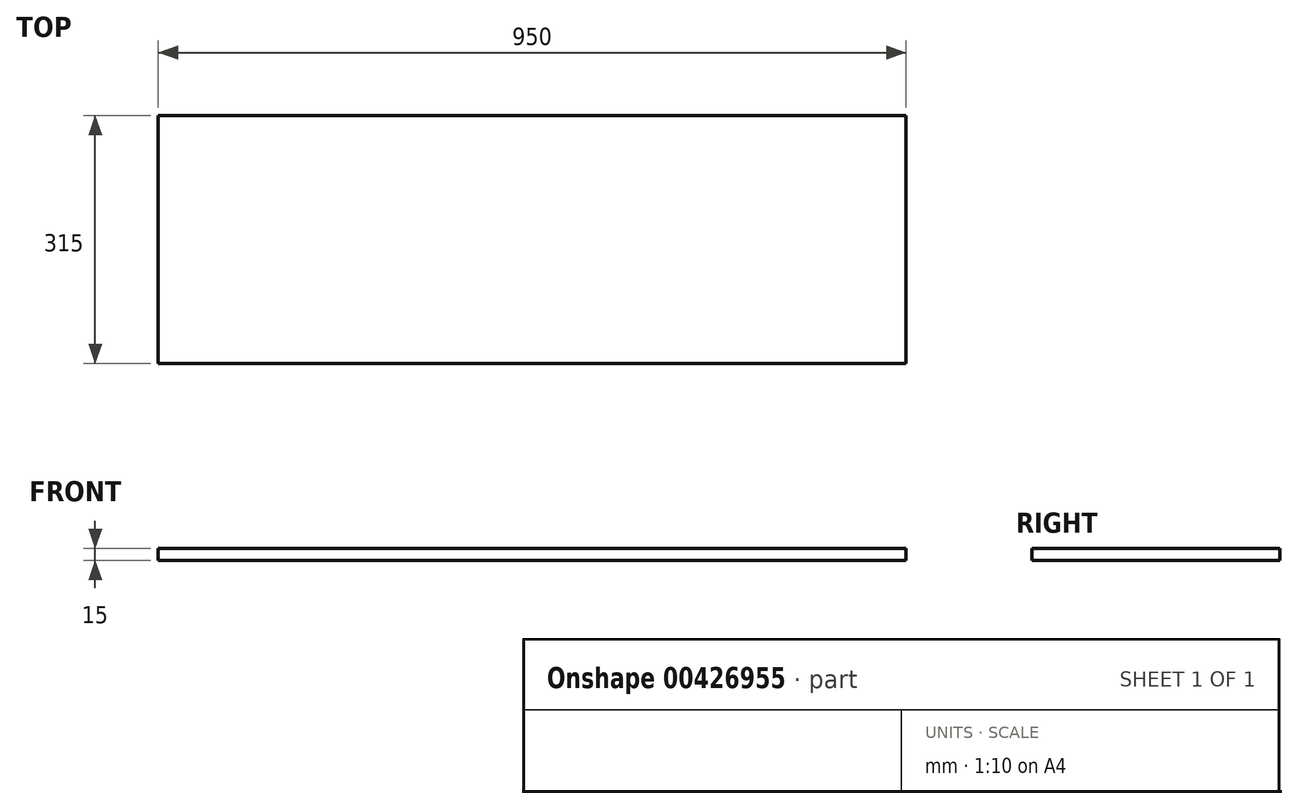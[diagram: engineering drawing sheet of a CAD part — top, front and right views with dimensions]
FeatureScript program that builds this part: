
annotation { "Feature Type Name" : "Feature", "Feature Type Description" : "" }
export const myFeature = defineFeature(function(context is Context, id is Id, definition is map)
    precondition{}
    {
        {
            var Q0;
            Q0=qCreatedBy(makeId("Top.planeOp"),FACE);
            var sketch = newSketch(context, id + "F0", { "sketchPlane" : qUnion([Q0])});
            skLineSegment(sketch, "E0.bottom", {"start": v(-222.47, 149.68) * mm, "end": v(727.53, 149.68) * mm});
            skLineSegment(sketch, "E0.top", {"start": v(-222.47, -165.32) * mm, "end": v(727.53, -165.32) * mm});
            skLineSegment(sketch, "E0.left", {"start": v(-222.47, 149.68) * mm, "end": v(-222.47, -165.32) * mm});
            skLineSegment(sketch, "E0.right", {"start": v(727.53, 149.68) * mm, "end": v(727.53, -165.32) * mm});
            skSolve(sketch);
        }
        {
            var Q0;
            Q0=makeQuery(id+"F0.imprint","IMPRINT",FACE,{"disambiguationData":[TD([[makeQuery(id+"F0.imprint","IMPRINT",EDGE,{"derivedFrom":sQuery(id+"F0.wireOp",EDGE,"E0.bottom")}),-1.0]])]});
            extrude(context, id + "F1", {"entities" : qUnion([Q0]), "depth" : 15 * mm});
        }
    });
